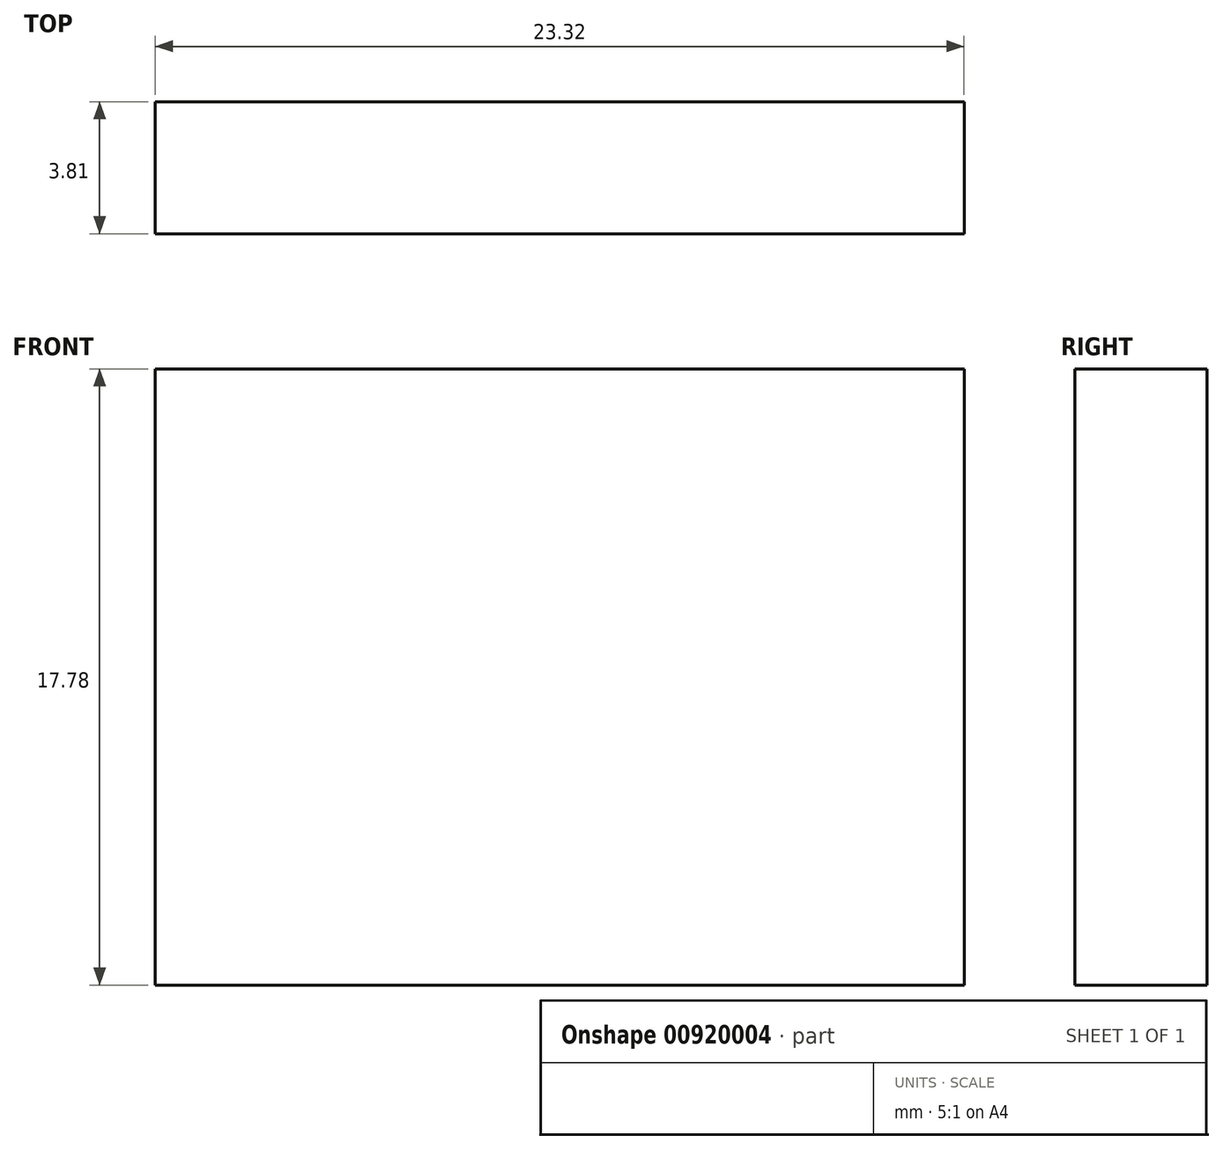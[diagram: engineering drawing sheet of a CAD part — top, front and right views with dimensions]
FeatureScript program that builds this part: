
annotation { "Feature Type Name" : "Feature", "Feature Type Description" : "" }
export const myFeature = defineFeature(function(context is Context, id is Id, definition is map)
    precondition{}
    {
        {
            var Q0;
            Q0=qCreatedBy(makeId("Front.planeOp"),FACE);
            var sketch = newSketch(context, id + "F0", { "sketchPlane" : qUnion([Q0])});
            skLineSegment(sketch, "E0.bottom", {"start": v(-11.95, 7.38) * mm, "end": v(11.37, 7.38) * mm});
            skLineSegment(sketch, "E0.top", {"start": v(-11.95, -10.4) * mm, "end": v(11.37, -10.4) * mm});
            skLineSegment(sketch, "E0.left", {"start": v(-11.95, 7.38) * mm, "end": v(-11.95, -10.4) * mm});
            skLineSegment(sketch, "E0.right", {"start": v(11.37, 7.38) * mm, "end": v(11.37, -10.4) * mm});
            skSolve(sketch);
        }
        {
            var Q0;
            Q0=makeQuery(id+"F0.imprint","IMPRINT",FACE,{"disambiguationData":[TD([[makeQuery(id+"F0.imprint","IMPRINT",EDGE,{"derivedFrom":sQuery(id+"F0.wireOp",EDGE,"E0.bottom")}),-1.0]])]});
            extrude(context, id + "F1", {"entities" : qUnion([Q0]), "depth" : 3.8 * mm, "offsetDistance" : 25.4 * mm});
        }
    });
